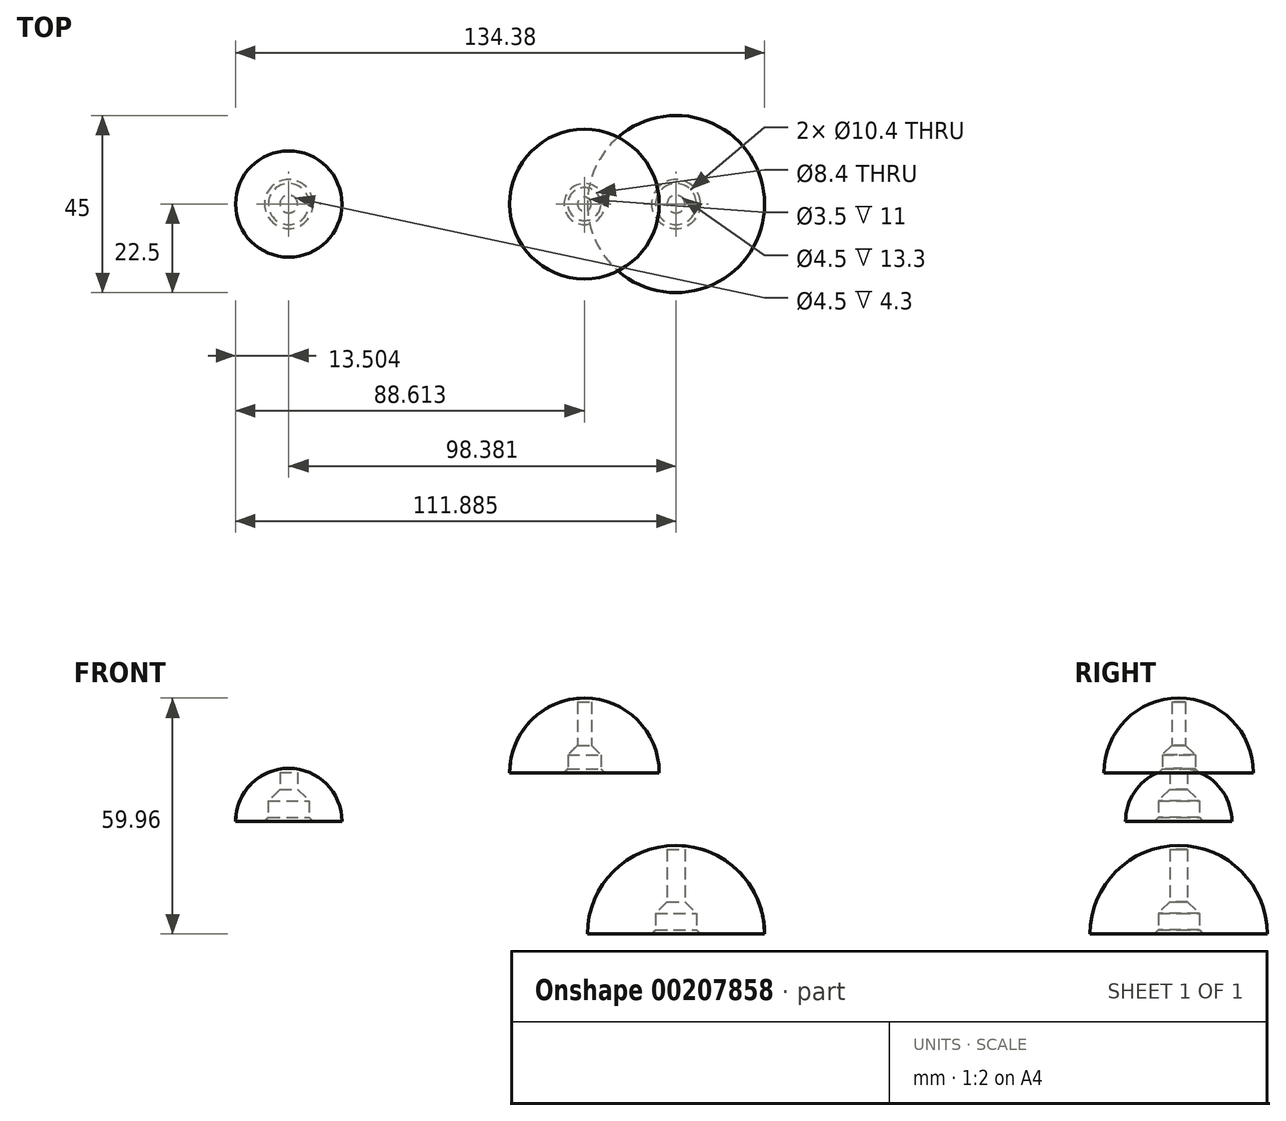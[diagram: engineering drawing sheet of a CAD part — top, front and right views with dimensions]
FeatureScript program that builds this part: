
annotation { "Feature Type Name" : "Feature", "Feature Type Description" : "" }
export const myFeature = defineFeature(function(context is Context, id is Id, definition is map)
    precondition{}
    {
        {
            var Q0;
            Q0=qCreatedBy(makeId("Front.planeOp"),FACE);
            var sketch = newSketch(context, id + "F0", { "sketchPlane" : qUnion([Q0])});
            skLineSegment(sketch, "E0", {"start": v(-98.93, 22.2) * mm, "end": v(-85.43, 22.2) * mm, "construction": true});
            skLineSegment(sketch, "E1", {"start": v(-85.43, 22.2) * mm, "end": v(-85.43, 35.7) * mm, "construction": true});
            skLineSegment(sketch, "E2", {"start": v(-85.43, 35.7) * mm, "end": v(-85.43, 34.7) * mm});
            skLineSegment(sketch, "E3", {"start": v(-85.43, 34.7) * mm, "end": v(-87.68, 34.7) * mm});
            skLineSegment(sketch, "E4", {"start": v(-87.68, 34.7) * mm, "end": v(-87.68, 27.4) * mm});
            skLineSegment(sketch, "E5", {"start": v(-87.68, 27.4) * mm, "end": v(-90.63, 27.4) * mm});
            skLineSegment(sketch, "E6", {"start": v(-90.63, 27.4) * mm, "end": v(-90.63, 22.2) * mm});
            skLineSegment(sketch, "E7", {"start": v(-90.63, 22.2) * mm, "end": v(-98.93, 22.2) * mm});
            skArc(sketch, "E8", {"start": v(-98.93, 22.2) * mm, "mid": v(-94.97, 31.75) * mm, "end": v(-85.43, 35.7) * mm});
            skSolve(sketch);
        }
        {
            var Q0;
            Q0 = qSketchRegion(id + "F0", true);
            var Q1;
            Q1=sQuery(id+"F0.wireOp",EDGE,"E1");
            revolve(context, id + "F1", {"entities" : qUnion([Q0]), "axis" : qUnion([Q1]), "revolveType" : RevolveType.FULL});
        }
        {
            var Q0;
            Q0=qCreatedBy(makeId("Front.planeOp"),FACE);
            var sketch = newSketch(context, id + "F2", { "sketchPlane" : qUnion([Q0])});
            skLineSegment(sketch, "E9", {"start": v(-9.55, -6.39) * mm, "end": v(12.95, -6.39) * mm, "construction": true});
            skLineSegment(sketch, "E10", {"start": v(12.95, -6.39) * mm, "end": v(12.95, 16.11) * mm, "construction": true});
            skLineSegment(sketch, "E11", {"start": v(12.95, 16.11) * mm, "end": v(12.95, 15.11) * mm});
            skLineSegment(sketch, "E12", {"start": v(12.95, 15.11) * mm, "end": v(10.7, 15.11) * mm});
            skLineSegment(sketch, "E13", {"start": v(10.7, 15.11) * mm, "end": v(10.7, -1.19) * mm});
            skLineSegment(sketch, "E14", {"start": v(10.7, -1.19) * mm, "end": v(7.75, -1.19) * mm});
            skLineSegment(sketch, "E15", {"start": v(7.75, -1.19) * mm, "end": v(7.75, -6.39) * mm});
            skLineSegment(sketch, "E16", {"start": v(7.75, -6.39) * mm, "end": v(-9.55, -6.39) * mm});
            skArc(sketch, "E17", {"start": v(-9.55, -6.39) * mm, "mid": v(-2.95, 9.52) * mm, "end": v(12.95, 16.11) * mm});
            skSolve(sketch);
        }
        {
            var Q0;
            Q0 = qSketchRegion(id + "F2", true);
            var Q1;
            Q1=sQuery(id+"F2.wireOp",EDGE,"E10");
            revolve(context, id + "F3", {"entities" : qUnion([Q0]), "axis" : qUnion([Q1]), "revolveType" : RevolveType.FULL});
        }
        {
            var Q0;
            Q0=qCreatedBy(makeId("Front.planeOp"),FACE);
            var sketch = newSketch(context, id + "F4", { "sketchPlane" : qUnion([Q0])});
            skLineSegment(sketch, "E18", {"start": v(-29.32, 34.57) * mm, "end": v(-10.32, 34.57) * mm, "construction": true});
            skLineSegment(sketch, "E19", {"start": v(-10.32, 34.57) * mm, "end": v(-10.32, 53.57) * mm, "construction": true});
            skLineSegment(sketch, "E20", {"start": v(-10.32, 53.57) * mm, "end": v(-10.32, 52.57) * mm});
            skLineSegment(sketch, "E21", {"start": v(-10.32, 52.57) * mm, "end": v(-12.07, 52.57) * mm});
            skLineSegment(sketch, "E22", {"start": v(-12.07, 52.57) * mm, "end": v(-12.07, 38.57) * mm});
            skLineSegment(sketch, "E23", {"start": v(-12.07, 38.57) * mm, "end": v(-14.52, 38.57) * mm});
            skLineSegment(sketch, "E24", {"start": v(-14.52, 38.57) * mm, "end": v(-14.52, 34.57) * mm});
            skLineSegment(sketch, "E25", {"start": v(-14.52, 34.57) * mm, "end": v(-29.32, 34.57) * mm});
            skArc(sketch, "E26", {"start": v(-29.32, 34.57) * mm, "mid": v(-23.75, 48) * mm, "end": v(-10.32, 53.57) * mm});
            skSolve(sketch);
        }
        {
            var Q0;
            Q0 = qSketchRegion(id + "F4", true);
            var Q1;
            Q1=sQuery(id+"F4.wireOp",EDGE,"E19");
            revolve(context, id + "F5", {"entities" : qUnion([Q0]), "axis" : qUnion([Q1]), "revolveType" : RevolveType.FULL});
        }
        {
            var Q0;
            Q0=makeQuery(id+"F1.opRevolve","SWEPT_EDGE",EDGE,{"disambiguationData":[OSD([sQuery(id+"F0.wireOp",EDGE,"E4"),sQuery(id+"F0.wireOp",EDGE,"E5")])]});
            var Q1;
            Q1=makeQuery(id+"F3.opRevolve","SWEPT_EDGE",EDGE,{"disambiguationData":[OSD([sQuery(id+"F2.wireOp",EDGE,"E13"),sQuery(id+"F2.wireOp",EDGE,"E14")])]});
            var Q2;
            Q2=makeQuery(id+"F5.opRevolve","SWEPT_EDGE",EDGE,{"disambiguationData":[OSD([sQuery(id+"F4.wireOp",EDGE,"E22"),sQuery(id+"F4.wireOp",EDGE,"E23")])]});
            chamfer(context, id + "F6", {"entities" : qUnion([Q0, Q1, Q2]), "width" : 3 * mm, "tangentPropagation" : true});
        }
        {
            var Q0;
            Q0=makeQuery(id+"F1.opRevolve","SWEPT_EDGE",EDGE,{"disambiguationData":[OSD([sQuery(id+"F0.wireOp",EDGE,"E6"),sQuery(id+"F0.wireOp",EDGE,"E7")])]});
            var Q1;
            Q1=makeQuery(id+"F5.opRevolve","SWEPT_EDGE",EDGE,{"disambiguationData":[OSD([sQuery(id+"F4.wireOp",EDGE,"E24"),sQuery(id+"F4.wireOp",EDGE,"E25")])]});
            var Q2;
            Q2=makeQuery(id+"F3.opRevolve","SWEPT_EDGE",EDGE,{"disambiguationData":[OSD([sQuery(id+"F2.wireOp",EDGE,"E15"),sQuery(id+"F2.wireOp",EDGE,"E16")])]});
            chamfer(context, id + "F7", {"entities" : qUnion([Q0, Q1, Q2]), "width" : 1 * mm, "tangentPropagation" : true});
        }
    });
